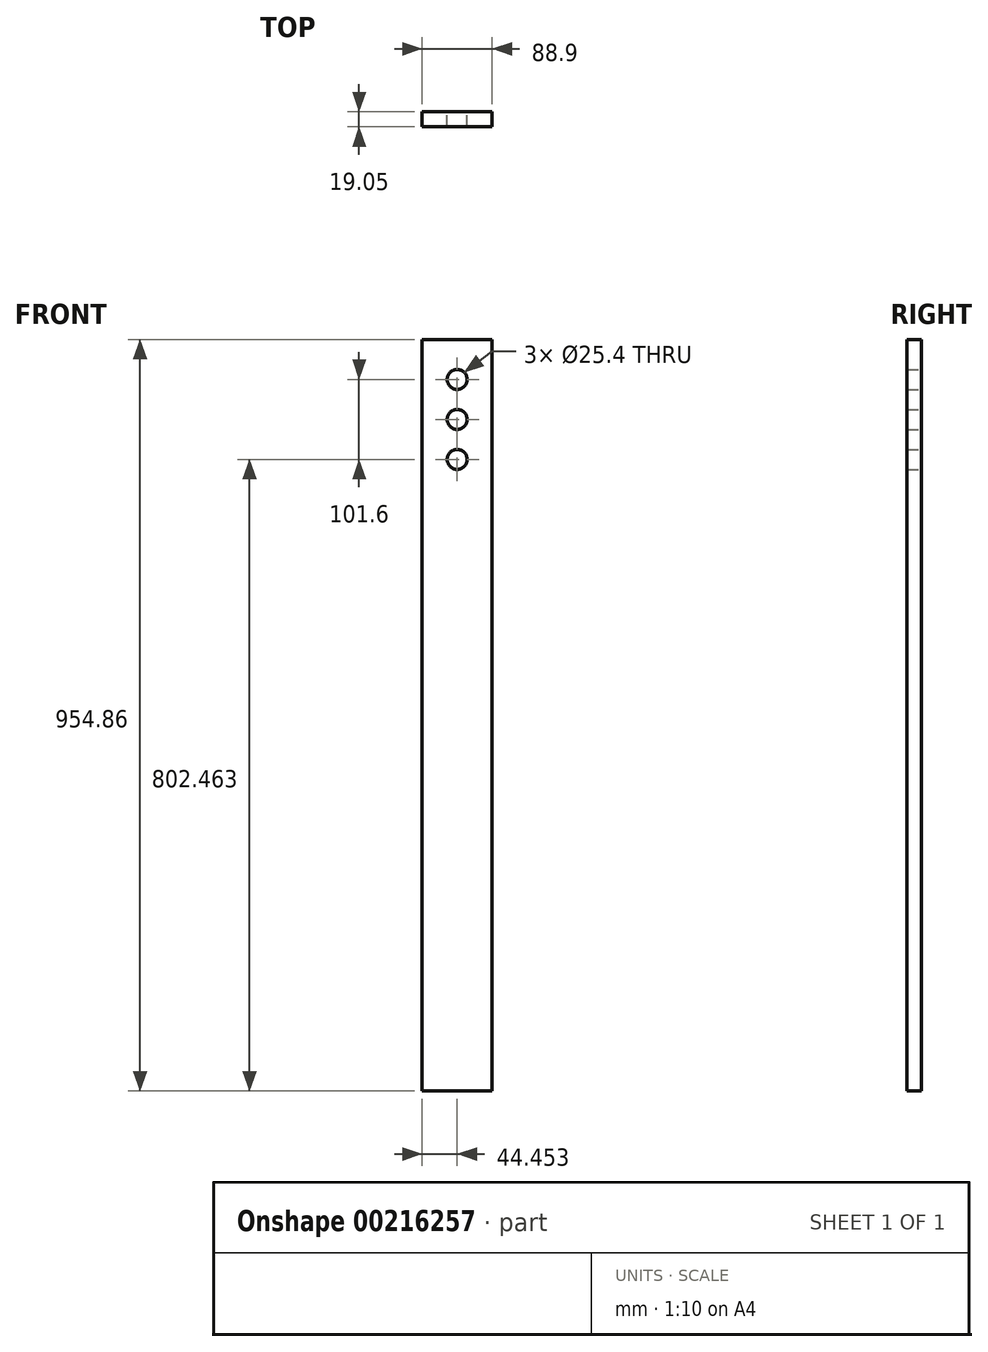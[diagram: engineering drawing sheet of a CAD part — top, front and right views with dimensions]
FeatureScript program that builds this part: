
annotation { "Feature Type Name" : "Feature", "Feature Type Description" : "" }
export const myFeature = defineFeature(function(context is Context, id is Id, definition is map)
    precondition{}
    {
        {
            var Q0;
            Q0=qCreatedBy(makeId("Front.planeOp"),FACE);
            var sketch = newSketch(context, id + "F0", { "sketchPlane" : qUnion([Q0])});
            skLineSegment(sketch, "E0", {"start": v(-4238.85, -1755.55) * mm, "end": v(-4143.6, -1755.55) * mm});
            skLineSegment(sketch, "E1", {"start": v(-4146.78, -1755.55) * mm, "end": v(-4146.78, -800.69) * mm});
            skLineSegment(sketch, "E2", {"start": v(-4143.6, -800.69) * mm, "end": v(-4238.85, -800.69) * mm});
            skLineSegment(sketch, "E3", {"start": v(-4235.68, -800.69) * mm, "end": v(-4235.68, -1755.55) * mm});
            skCircle(sketch, "E4", {"center": v(-4191.23, -851.49) * mm, "radius": 12.7 * mm});
            skCircle(sketch, "E5", {"center": v(-4191.23, -902.29) * mm, "radius": 12.7 * mm});
            skCircle(sketch, "E6", {"center": v(-4191.23, -953.09) * mm, "radius": 12.7 * mm});
            skSolve(sketch);
        }
        {
            var Q0;
            Q0=makeQuery(id+"F0.imprint","IMPRINT",FACE,{"disambiguationData":[TD([[makeQuery(id+"F0.imprint","IMPRINT",EDGE,{"derivedFrom":sQuery(id+"F0.wireOp",EDGE,"E0")}),1.0]])]});
            extrude(context, id + "F1", {"entities" : qUnion([Q0]), "depth" : 19.05 * mm});
        }
    });
